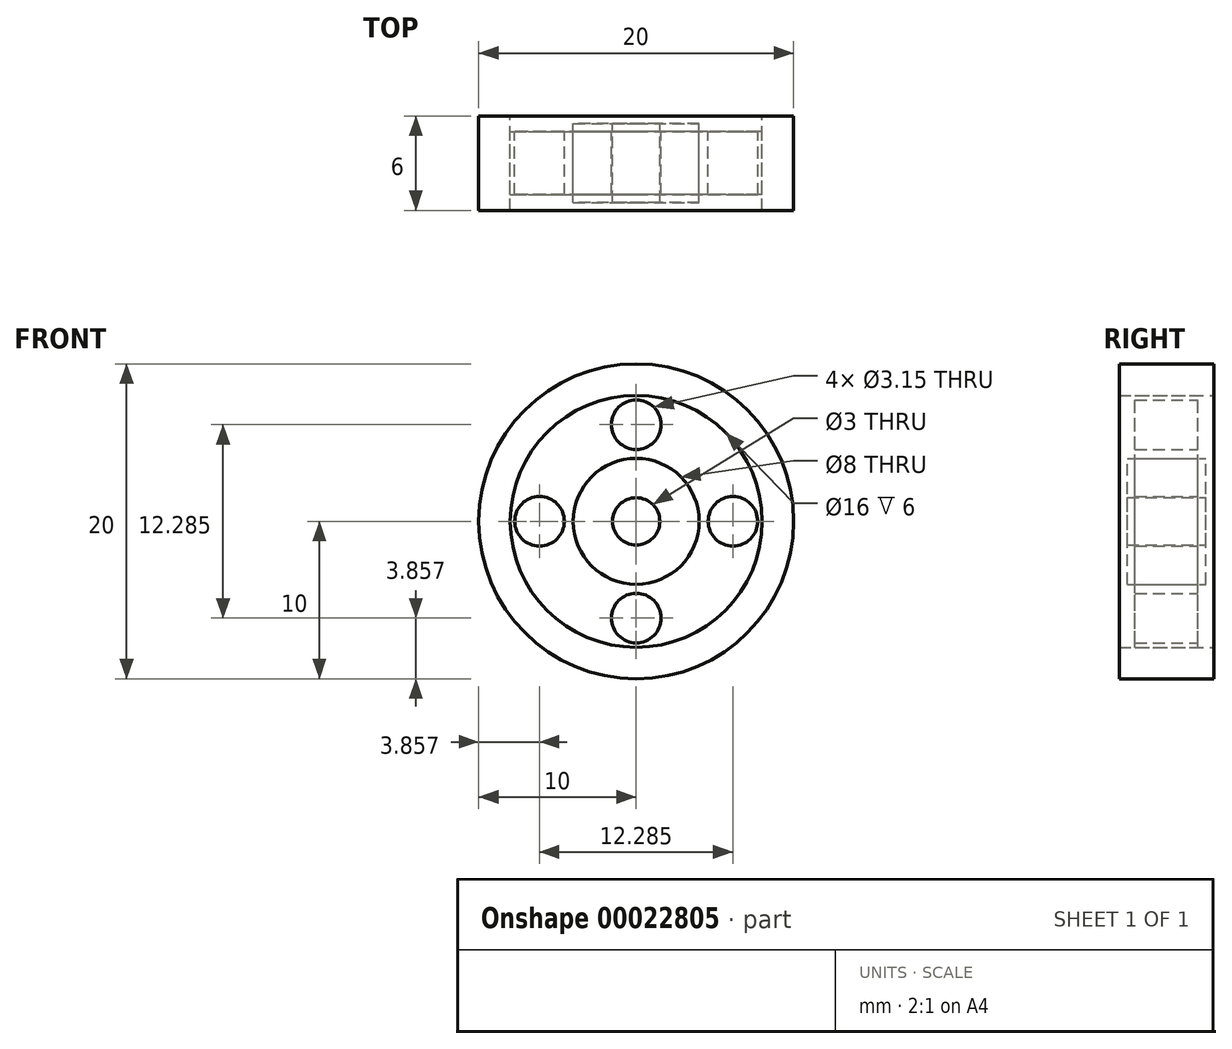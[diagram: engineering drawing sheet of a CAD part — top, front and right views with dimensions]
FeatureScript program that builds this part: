
annotation { "Feature Type Name" : "Feature", "Feature Type Description" : "" }
export const myFeature = defineFeature(function(context is Context, id is Id, definition is map)
    precondition{}
    {
        {
            var Q0;
            Q0=qCreatedBy(makeId("Front.planeOp"),FACE);
            var sketch = newSketch(context, id + "F0", { "sketchPlane" : qUnion([Q0])});
            skCircle(sketch, "E0", {"center": v(0, 0) * mm, "radius": 8 * mm});
            skCircle(sketch, "E1", {"center": v(0, 0) * mm, "radius": 1.5 * mm});
            skCircle(sketch, "E2", {"center": v(0, 0) * mm, "radius": 4 * mm});
            skCircle(sketch, "E3", {"center": v(0, 0) * mm, "radius": 10 * mm});
            skCircle(sketch, "E4", {"center": v(0, 6.14) * mm, "radius": 1.57 * mm});
            skCircle(sketch, "E5.1.0", {"center": v(-6.14, 0) * mm, "radius": 1.57 * mm});
            skCircle(sketch, "E5.2.0", {"center": v(0, -6.14) * mm, "radius": 1.57 * mm});
            skCircle(sketch, "E5.3.0", {"center": v(6.14, 0) * mm, "radius": 1.57 * mm});
            skSolve(sketch);
        }
        {
            var Q0;
            Q0=makeQuery(id+"F0.imprint","IMPRINT",FACE,{"disambiguationData":[TD([[makeQuery(id+"F0.imprint","IMPRINT",EDGE,{"derivedFrom":sQuery(id+"F0.wireOp",EDGE,"E0")}),-1.0]])]});
            extrude(context, id + "F1", {"entities" : qUnion([Q0]), "endBound" : BoundingType.SYMMETRIC, "depth" : 6 * mm});
        }
        {
            var Q0;
            Q0=makeQuery(id+"F0.imprint","IMPRINT",FACE,{"disambiguationData":[TD([[makeQuery(id+"F0.imprint","IMPRINT",EDGE,{"derivedFrom":sQuery(id+"F0.wireOp",EDGE,"E1")}),-1.0]])]});
            extrude(context, id + "F2", {"entities" : qUnion([Q0]), "endBound" : BoundingType.SYMMETRIC, "depth" : 5 * mm});
        }
        {
            var Q0;
            Q0=makeQuery(id+"F0.imprint","IMPRINT",FACE,{"disambiguationData":[TD([[makeQuery(id+"F0.imprint","IMPRINT",EDGE,{"derivedFrom":sQuery(id+"F0.wireOp",EDGE,"E0")}),1.0]])]});
            extrude(context, id + "F3", {"entities" : qUnion([Q0]), "endBound" : BoundingType.SYMMETRIC, "depth" : 4 * mm});
        }
    });
